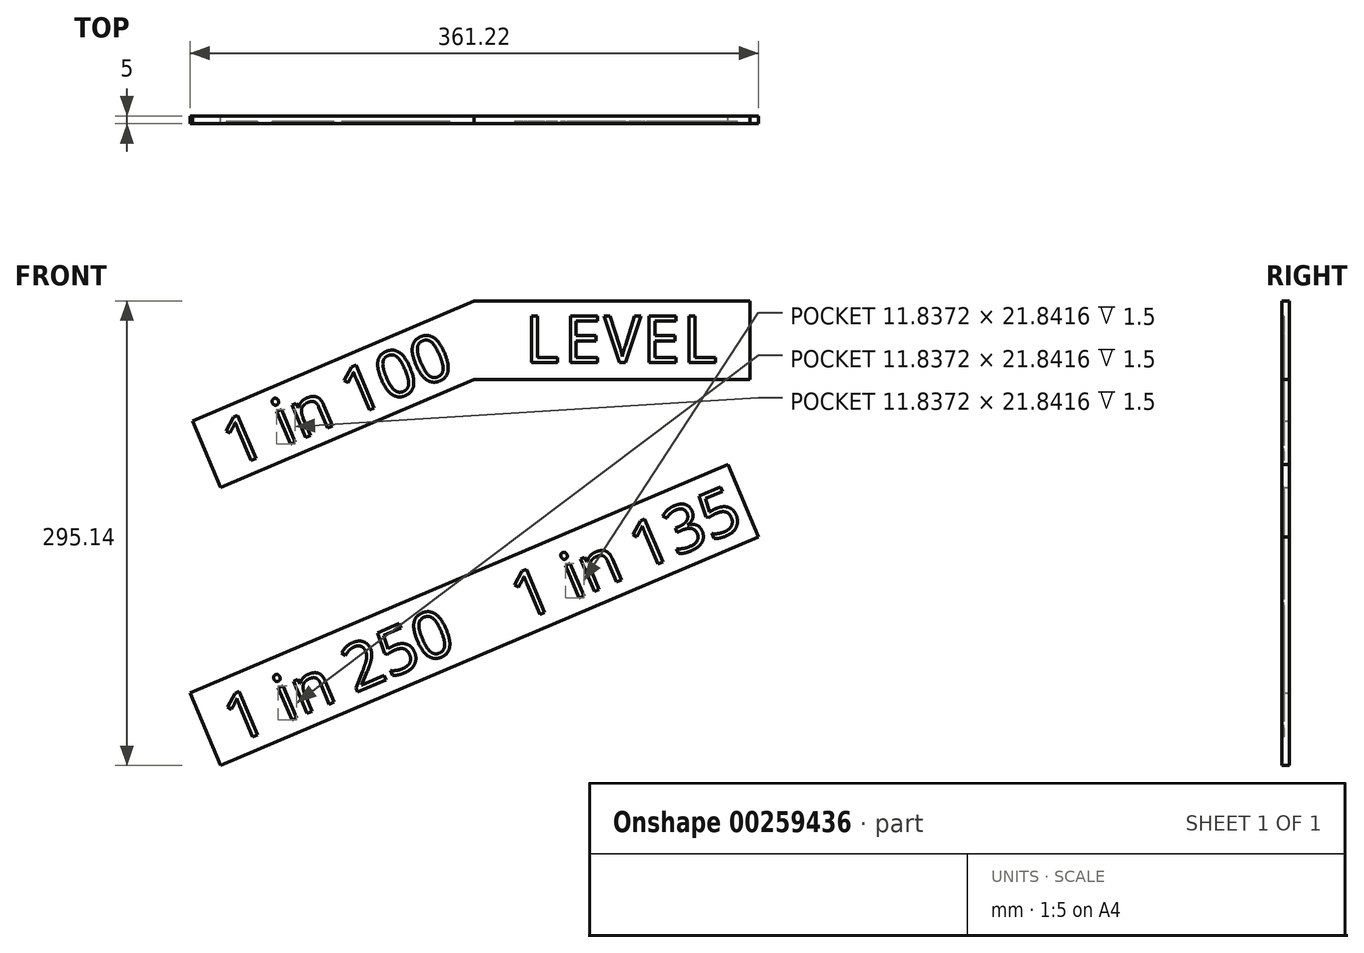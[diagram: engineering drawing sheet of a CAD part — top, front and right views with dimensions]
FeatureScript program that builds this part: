
annotation { "Feature Type Name" : "Feature", "Feature Type Description" : "" }
export const myFeature = defineFeature(function(context is Context, id is Id, definition is map)
    precondition{}
    {
        {
            var Q0;
            Q0=qCreatedBy(makeId("Front.planeOp"),FACE);
            var sketch = newSketch(context, id + "F0", { "sketchPlane" : qUnion([Q0])});
            skLineSegment(sketch, "E0.bottom", {"start": v(0, 0) * mm, "end": v(175, 0) * mm});
            skLineSegment(sketch, "E0.top", {"start": v(0, 50) * mm, "end": v(175, 50) * mm});
            skLineSegment(sketch, "E0.left", {"start": v(0, 0) * mm, "end": v(0, 50) * mm});
            skLineSegment(sketch, "E0.right", {"start": v(175, 0) * mm, "end": v(175, 50) * mm});
            skLineSegment(sketch, "E1", {"start": v(0, 0) * mm, "end": v(-161.04, -68.5) * mm});
            skLineSegment(sketch, "E2", {"start": v(-161.04, -68.5) * mm, "end": v(-179.05, -26.16) * mm});
            skLineSegment(sketch, "E3", {"start": v(0, 50) * mm, "end": v(-179.05, -26.16) * mm});
            skSolve(sketch);
        }
        {
            var Q0;
            Q0=qSketchRegion(id+"F0",true);
            extrude(context, id + "F1", {"entities" : qUnion([Q0]), "depth" : 5 * mm, "offsetDistance" : 25 * mm});
        }
        {
            var Q0;
            Q0=makeQuery(id+"F1.opExtrude","CAP_FACE",FACE,{"disambiguationData":[OSD([sQuery(id+"F0.wireOp",EDGE,"E0.bottom"),sQuery(id+"F0.wireOp",EDGE,"E0.top"),sQuery(id+"F0.wireOp",EDGE,"E0.right"),sQuery(id+"F0.wireOp",EDGE,"E1"),sQuery(id+"F0.wireOp",EDGE,"E2"),sQuery(id+"F0.wireOp",EDGE,"E3")])],"isStart":false});
            var sketch = newSketch(context, id + "F2", { "sketchPlane" : qUnion([Q0])});
            skText(sketch, "E4", { "text": "LEVEL", "fontName": "DroidSansMono.ttf"});
            skText(sketch, "E5", { "text": "1 in 100", "fontName": "OpenSans-Regular.ttf"});
            const initialGuessF2  = {"E4": [0.03157, 0.01076, 1, 0, 0.03], "E5": [-0.152, -0.05574, 0.92021, 0.39142, 0.03]};
            skSetInitialGuess(sketch, initialGuessF2);
            skSolve(sketch);
        }
        {
            var Q0;
            Q0=qSketchRegion(id+"F2",true);
            extrude(context, id + "F3", {"entities" : qUnion([Q0]), "operationType" : NewBodyOperationType.REMOVE, "oppositeDirection" : true, "depth" : 1.5 * mm, "offsetDistance" : 25 * mm});
        }
        {
            var Q0;
            Q0=qCreatedBy(makeId("Front.planeOp"),FACE);
            var sketch = newSketch(context, id + "F4", { "sketchPlane" : qUnion([Q0])});
            skLineSegment(sketch, "E6", {"start": v(0, 65.24) * mm, "end": v(0, 115.24) * mm});
            skLineSegment(sketch, "E7", {"start": v(0, 115.24) * mm, "end": v(164.45, 175.1) * mm});
            skLineSegment(sketch, "E8.MirrorCS", {"start": v(0, 115.24) * mm, "end": v(-164.45, 175.1) * mm});
            skLineSegment(sketch, "E9.MirrorCS", {"start": v(-180.52, 130.95) * mm, "end": v(0, 65.24) * mm});
            skLineSegment(sketch, "E10", {"start": v(-164.45, 175.1) * mm, "end": v(-180.52, 130.95) * mm});
            skPoint(sketch, "E11.orphan", {"position": v(-164.45, 125.1) * mm});
            skPoint(sketch, "E12.end.orphan", {"position": v(164.45, 125.1) * mm});
            skLineSegment(sketch, "E13.MirrorCS", {"start": v(164.45, 175.1) * mm, "end": v(180.52, 130.95) * mm});
            skLineSegment(sketch, "E14.MirrorCS", {"start": v(180.52, 130.95) * mm, "end": v(0, 65.24) * mm});
            skSolve(sketch);
        }
        {
            var Q0;
            Q0=qSketchRegion(id+"F4",true);
            extrude(context, id + "F5", {"entities" : qUnion([Q0]), "oppositeDirection" : true, "depth" : 5 * mm, "offsetDistance" : 25 * mm});
        }
        {
            var Q0;
            Q0=makeQuery(id+"F5.opExtrude","CAP_FACE",FACE,{"disambiguationData":[OSD([sQuery(id+"F4.wireOp",EDGE,"E7"),sQuery(id+"F4.wireOp",EDGE,"E8.MirrorCS"),sQuery(id+"F4.wireOp",EDGE,"E9.MirrorCS"),sQuery(id+"F4.wireOp",EDGE,"E10"),sQuery(id+"F4.wireOp",EDGE,"E13.MirrorCS"),sQuery(id+"F4.wireOp",EDGE,"E14.MirrorCS")])],"isStart":true});
            var sketch = newSketch(context, id + "F6", { "sketchPlane" : qUnion([Q0])});
            skText(sketch, "E15", { "text": "1 in 100", "fontName": "OpenSans-Regular.ttf"});
            skText(sketch, "E16", { "text": "1 in 150", "fontName": "OpenSans-Regular.ttf"});
            const initialGuessF6  = {"E15": [0.01823, 0.08139, 0.9397, 0.34202, 0.03], "E16": [-0.1607, 0.13266, 0.9397, -0.34202, 0.03]};
            skSetInitialGuess(sketch, initialGuessF6);
            skSolve(sketch);
        }
        {
            var Q0;
            Q0=qSketchRegion(id+"F6",true);
            extrude(context, id + "F7", {"entities" : qUnion([Q0]), "operationType" : NewBodyOperationType.REMOVE, "oppositeDirection" : true, "depth" : 1.5 * mm, "offsetDistance" : 25 * mm});
        }
        {
            var Q0;
            Q0=qCreatedBy(makeId("Front.planeOp"),FACE);
            var sketch = newSketch(context, id + "F8", { "sketchPlane" : qUnion([Q0])});
            skLineSegment(sketch, "E17", {"start": v(0, -122.31) * mm, "end": v(0, -176.65) * mm});
            skLineSegment(sketch, "E18", {"start": v(0, -176.65) * mm, "end": v(-161.04, -245.14) * mm});
            skLineSegment(sketch, "E19.0", {"start": v(0, -122.31) * mm, "end": v(-180.6, -199.13) * mm});
            skPoint(sketch, "E20.orphan", {"position": v(0, -54.85) * mm});
            skLineSegment(sketch, "E21", {"start": v(-161.04, -245.14) * mm, "end": v(-180.6, -199.13) * mm});
            skLineSegment(sketch, "E22", {"start": v(0, -122.31) * mm, "end": v(161.04, -53.81) * mm});
            skLineSegment(sketch, "E23", {"start": v(161.04, -53.81) * mm, "end": v(180.6, -99.82) * mm});
            skLineSegment(sketch, "E24", {"start": v(180.6, -99.82) * mm, "end": v(0, -176.65) * mm});
            skSolve(sketch);
        }
        {
            var Q0;
            Q0=qSketchRegion(id+"F8",true);
            extrude(context, id + "F9", {"entities" : qUnion([Q0]), "depth" : 5 * mm, "offsetDistance" : 25 * mm});
        }
        {
            var Q0;
            Q0=makeQuery(id+"F9.opExtrude","CAP_FACE",FACE,{"disambiguationData":[OSD([sQuery(id+"F8.wireOp",EDGE,"E18"),sQuery(id+"F8.wireOp",EDGE,"E19.0"),sQuery(id+"F8.wireOp",EDGE,"E21"),sQuery(id+"F8.wireOp",EDGE,"E22"),sQuery(id+"F8.wireOp",EDGE,"E23"),sQuery(id+"F8.wireOp",EDGE,"E24")])],"isStart":false});
            var sketch = newSketch(context, id + "F10", { "sketchPlane" : qUnion([Q0])});
            skText(sketch, "E25", { "text": "1 in 250", "fontName": "OpenSans-Regular.ttf"});
            skText(sketch, "E26", { "text": "1 in 135", "fontName": "OpenSans-Regular.ttf"});
            const initialGuessF10  = {"E25": [-0.15102, -0.2312, 0.92021, 0.39142, 0.03], "E26": [0.03137, -0.15357, 0.92021, 0.39142, 0.03]};
            skSetInitialGuess(sketch, initialGuessF10);
            skSolve(sketch);
        }
        {
            var Q0;
            Q0=qSketchRegion(id+"F10",true);
            extrude(context, id + "F11", {"entities" : qUnion([Q0]), "operationType" : NewBodyOperationType.REMOVE, "oppositeDirection" : true, "depth" : 1.5 * mm, "offsetDistance" : 25 * mm});
        }
        {
            var Q0;
            Q0=makeQuery(id+"F5.opExtrude","SWEPT_BODY",BODY,{"disambiguationData":[OSD([sQuery(id+"F4.wireOp",EDGE,"E7"),sQuery(id+"F4.wireOp",EDGE,"E8.MirrorCS"),sQuery(id+"F4.wireOp",EDGE,"E9.MirrorCS"),sQuery(id+"F4.wireOp",EDGE,"E10"),sQuery(id+"F4.wireOp",EDGE,"E13.MirrorCS"),sQuery(id+"F4.wireOp",EDGE,"E14.MirrorCS")])]});
            deleteBodies(context, id + "F12", {"entities" : qUnion([Q0])});
        }
    });
